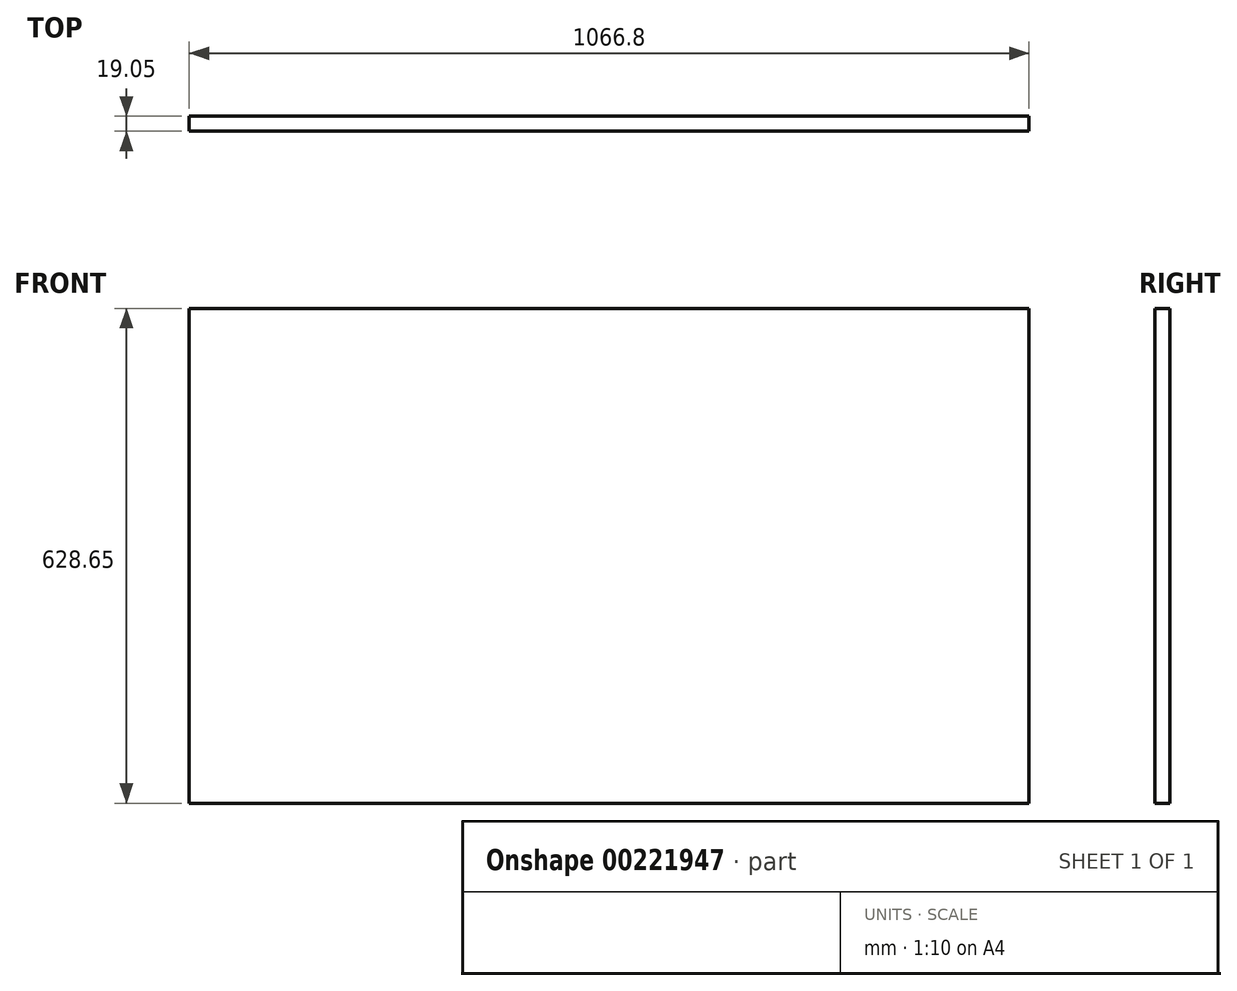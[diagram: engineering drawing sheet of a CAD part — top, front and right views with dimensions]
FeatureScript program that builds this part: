
annotation { "Feature Type Name" : "Feature", "Feature Type Description" : "" }
export const myFeature = defineFeature(function(context is Context, id is Id, definition is map)
    precondition{}
    {
        {
            var Q0;
            Q0=qCreatedBy(makeId("Front.planeOp"),FACE);
            var sketch = newSketch(context, id + "F0", { "sketchPlane" : qUnion([Q0])});
            skLineSegment(sketch, "E0.bottom", {"start": v(-1066.8, 344.32) * mm, "end": v(0, 344.32) * mm});
            skLineSegment(sketch, "E0.top", {"start": v(-1066.8, -284.33) * mm, "end": v(0, -284.33) * mm});
            skLineSegment(sketch, "E0.left", {"start": v(-1066.8, 344.32) * mm, "end": v(-1066.8, -284.33) * mm});
            skLineSegment(sketch, "E0.right", {"start": v(0, 344.32) * mm, "end": v(0, -284.33) * mm});
            skSolve(sketch);
        }
        {
            var Q0;
            Q0 = qSketchRegion(id + "F0", true);
            extrude(context, id + "F1", {"entities" : qUnion([Q0]), "depth" : 19.05 * mm});
        }
    });
